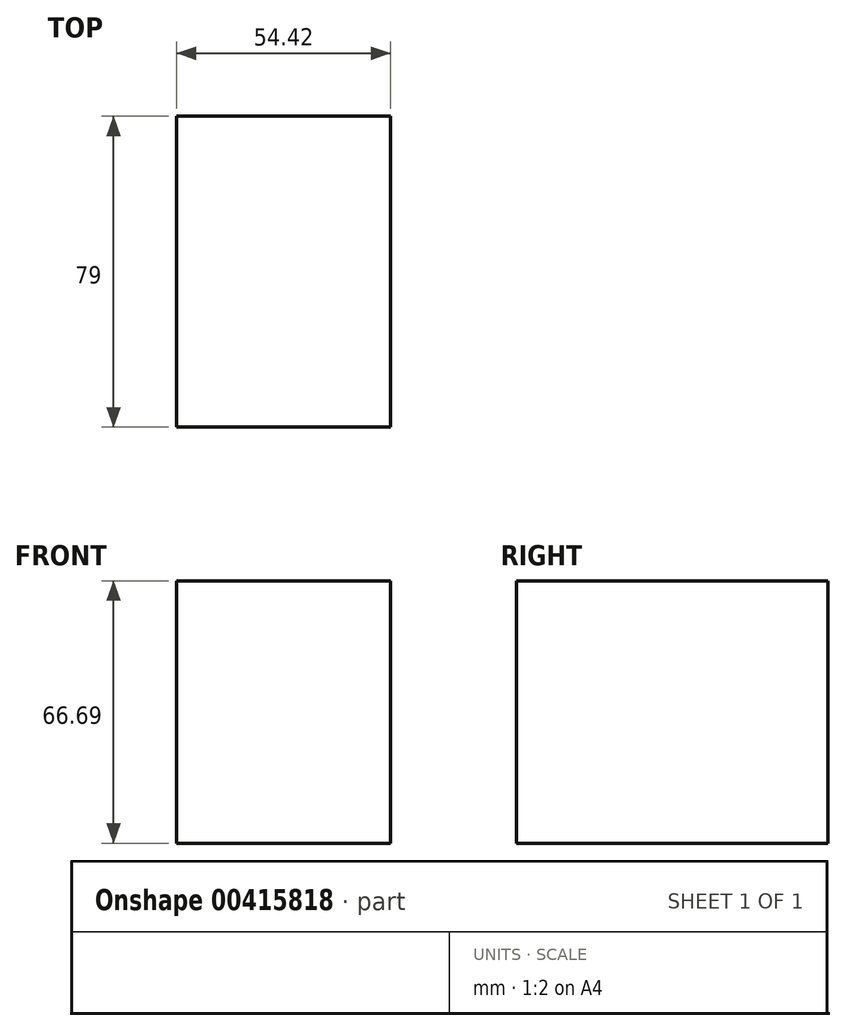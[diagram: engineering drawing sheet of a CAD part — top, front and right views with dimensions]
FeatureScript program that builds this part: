
annotation { "Feature Type Name" : "Feature", "Feature Type Description" : "" }
export const myFeature = defineFeature(function(context is Context, id is Id, definition is map)
    precondition{}
    {
        {
            var Q0;
            Q0=qCreatedBy(makeId("Front.planeOp"),FACE);
            var sketch = newSketch(context, id + "F0", { "sketchPlane" : qUnion([Q0])});
            skLineSegment(sketch, "E0.bottom", {"start": v(-27.2, 27.64) * mm, "end": v(27.2, 27.64) * mm});
            skLineSegment(sketch, "E0.top", {"start": v(-27.2, -39.05) * mm, "end": v(27.2, -39.05) * mm});
            skLineSegment(sketch, "E0.left", {"start": v(-27.2, 27.64) * mm, "end": v(-27.2, -39.05) * mm});
            skLineSegment(sketch, "E0.right", {"start": v(27.2, 27.64) * mm, "end": v(27.2, -39.05) * mm});
            skPoint(sketch, "E0.middle", {"position": v(0, -5.7) * mm});
            skSolve(sketch);
        }
        {
            var Q0;
            Q0=makeQuery(id+"F0.imprint","IMPRINT",FACE,{"disambiguationData":[TD([[makeQuery(id+"F0.imprint","IMPRINT",EDGE,{"derivedFrom":sQuery(id+"F0.wireOp",EDGE,"E0.bottom")}),-1.0]])]});
            extrude(context, id + "F1", {"entities" : qUnion([Q0]), "depth" : 79 * mm});
        }
    });
